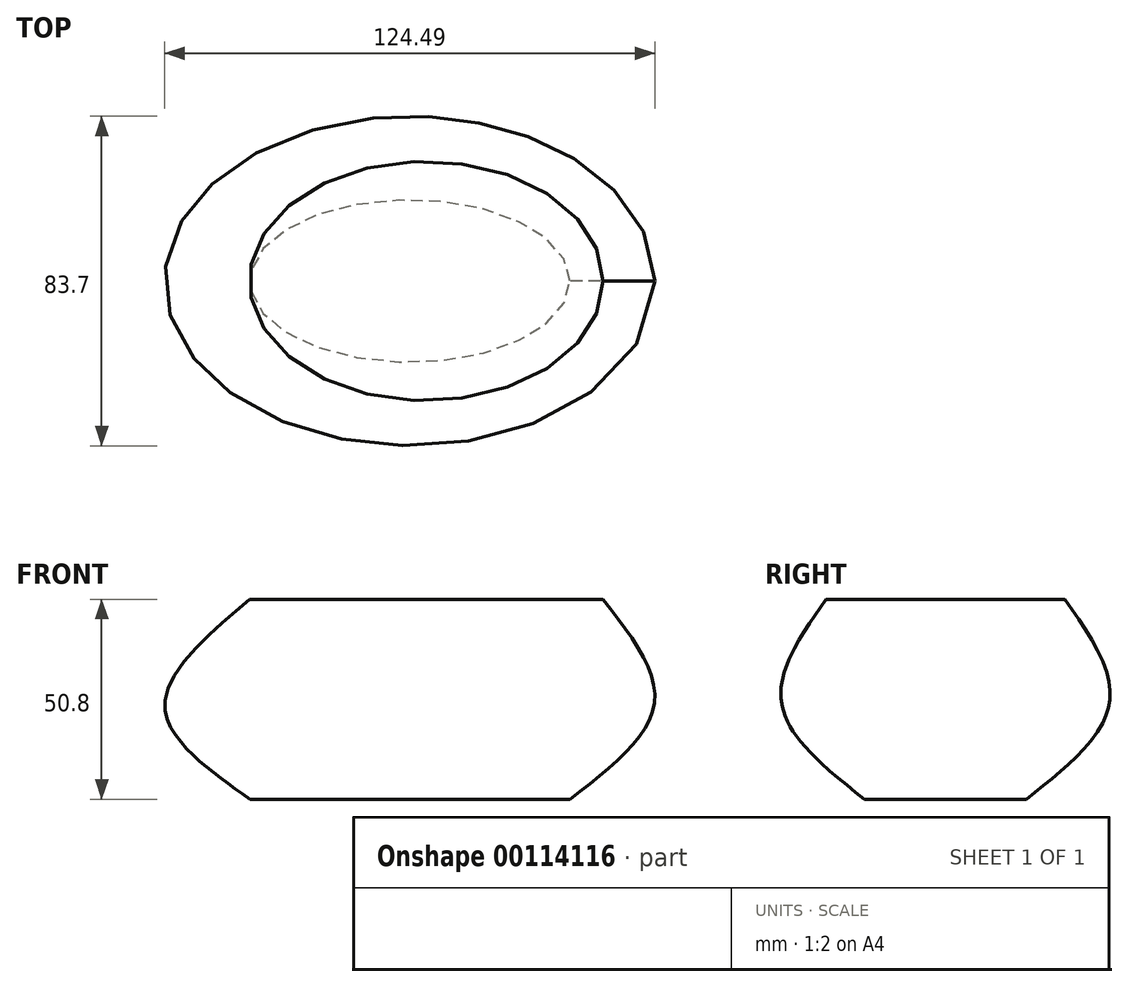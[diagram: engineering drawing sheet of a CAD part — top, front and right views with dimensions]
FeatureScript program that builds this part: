
annotation { "Feature Type Name" : "Feature", "Feature Type Description" : "" }
export const myFeature = defineFeature(function(context is Context, id is Id, definition is map)
    precondition{}
    {
        {
            var Q0;
            Q0=qCreatedBy(makeId("Top.planeOp"),FACE);
            var sketch = newSketch(context, id + "F0", { "sketchPlane" : qUnion([Q0])});
            skEllipse(sketch, "E0", {"center": v(0, 0) * mm, "majorRadius": 62.19 * mm, "minorRadius": 41.79 * mm, "majorAxis": v(1, 0)});
            skSolve(sketch);
        }
        {
            var Q0;
            Q0=qCreatedBy(makeId("Top.planeOp"),FACE);
            cPlane(context, id + "F1", {"entities" : qUnion([Q0]), "cplaneType" : CPlaneType.OFFSET, "offset" : 25.4 * mm, "width" : 152.4 * mm, "height" : 152.4 * mm});
        }
        {
            var Q0;
            Q0=qCreatedBy(id+"F1.planeOp",FACE);
            var sketch = newSketch(context, id + "F2", { "sketchPlane" : qUnion([Q0])});
            skEllipse(sketch, "E1", {"center": v(4.15, 0) * mm, "majorRadius": 44.91 * mm, "minorRadius": 30.4 * mm, "majorAxis": v(1, 0)});
            skSolve(sketch);
        }
        {
            var Q0;
            Q0=qCreatedBy(makeId("Top.planeOp"),FACE);
            cPlane(context, id + "F3", {"entities" : qUnion([Q0]), "cplaneType" : CPlaneType.OFFSET, "offset" : 25.4 * mm, "oppositeDirection" : true, "width" : 152.4 * mm, "height" : 152.4 * mm});
        }
        {
            var Q0;
            Q0=qCreatedBy(id+"F3.planeOp",FACE);
            var sketch = newSketch(context, id + "F4", { "sketchPlane" : qUnion([Q0])});
            skEllipse(sketch, "E2", {"center": v(0, 0) * mm, "majorRadius": 40.65 * mm, "minorRadius": 20.6 * mm, "majorAxis": v(1, 0)});
            skSolve(sketch);
        }
        {
            var Q0;
            Q0=makeQuery(id+"F2.imprint","IMPRINT",FACE,{"disambiguationData":[TD([[makeQuery(id+"F2.imprint","IMPRINT",EDGE,{"derivedFrom":sQuery(id+"F2.wireOp",EDGE,"E1")}),1.0]])]});
            var Q1;
            Q1=makeQuery(id+"F0.imprint","IMPRINT",FACE,{"disambiguationData":[TD([[makeQuery(id+"F0.imprint","IMPRINT",EDGE,{"derivedFrom":sQuery(id+"F0.wireOp",EDGE,"E0")}),1.0]])]});
            var Q2;
            Q2=makeQuery(id+"F4.imprint","IMPRINT",FACE,{"disambiguationData":[TD([[makeQuery(id+"F4.imprint","IMPRINT",EDGE,{"derivedFrom":sQuery(id+"F4.wireOp",EDGE,"E2")}),1.0]])]});
            loft(context, id + "F5", {"sheetProfilesArray" : [{ "sheetProfileEntities" : qUnion([Q0]) }, { "sheetProfileEntities" : qUnion([Q1]) }, { "sheetProfileEntities" : qUnion([Q2]) }]});
        }
    });
